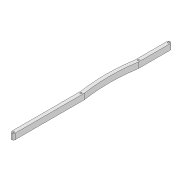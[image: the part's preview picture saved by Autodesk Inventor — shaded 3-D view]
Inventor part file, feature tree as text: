
AUTODESK INVENTOR PART (.ipt)
format: ipt  version: 2022 (Build 260153000, 153)  size: 115,200 bytes
history: native  units: mm
features: extrude x1, sketch x1
ambient origin geometry x8: Origin, YZ Plane, XZ Plane, XY Plane, X Axis, Y Axis, Z Axis, Center Point
bodies: Solid1 (feature_tree)
feature tree (2):
  extrude  "Extrusion1"  Depth=270.517mm
  sketch  "Sketch1"  dims[d0=6.0mm d1=270.517mm d2=3.0mm d3=3.0mm d4=10.0mm d5=0.0mm d10=3.0mm d11=117.696mm d12=3.0mm d13=217.699mm d22=2000.0mm d23=2000.0mm d24=3.0mm d25=3.0mm d26=3.0mm d27=3.0mm d28=0.2mm d29=100.0mm d30=100.0mm d31=60.0mm d33=60.0mm]
